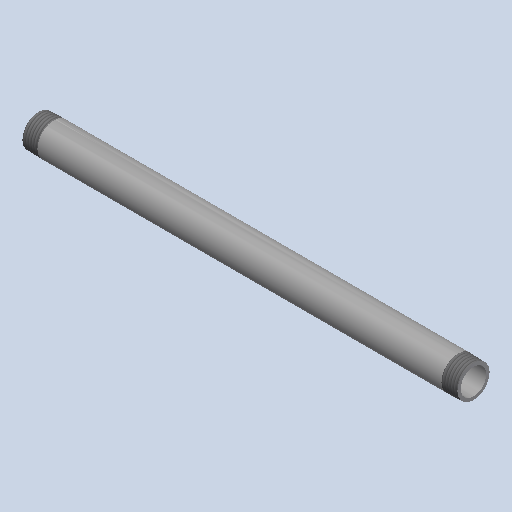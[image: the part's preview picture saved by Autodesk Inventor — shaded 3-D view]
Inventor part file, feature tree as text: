
AUTODESK INVENTOR PART (.ipt)
format: ipt  version: 2025 (Build 290162000, 162)  size: 177,664 bytes
history: native  units: mm (DEFAULTED — no unit token found)
features: other x8, revolve x1
ambient origin geometry x8: Origin, YZ Plane, XZ Plane, XY Plane, X Axis, Y Axis, Z Axis, Center Point
bodies: Solid1 (feature_tree)
feature tree (9):
  revolve  "Revolution1"  [1 undecoded]
  other  "Work Axis1"
  other  "Work Point5"
  other  "Work Axis2"
  other  "Work Point6"
  other  "Work Axis3"
  other  "Work Axis4"
  other  "Work Point7"
  other  "Work Point8"
note: 1 required parameter value undecoded (feature->parameter linkage not recoverable at this tier; creation-order binding heuristic only, values carry confidence <= 0.55)
